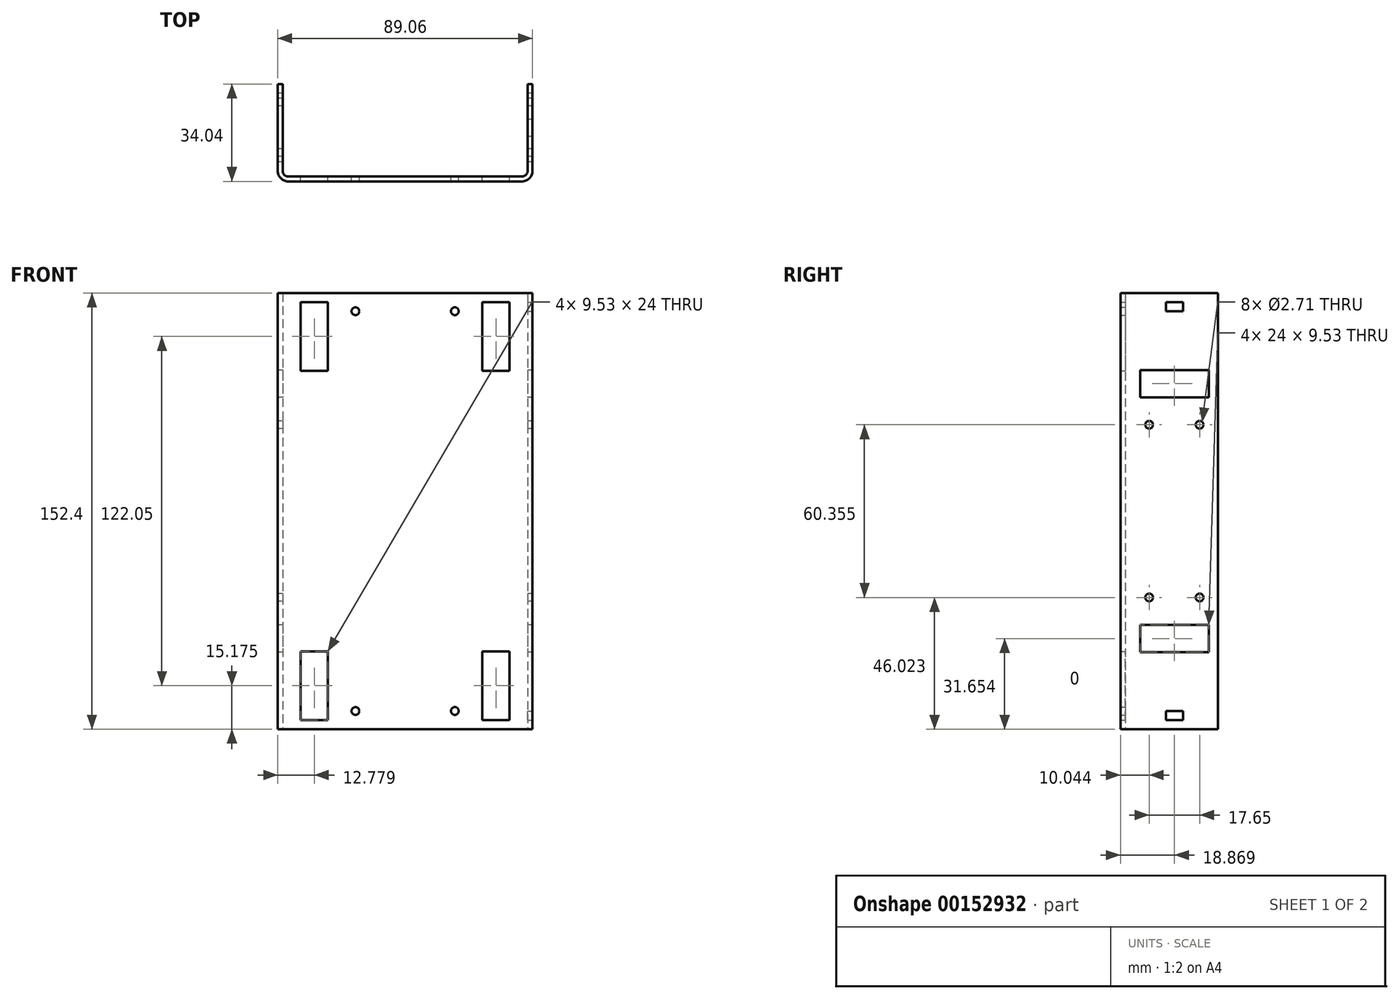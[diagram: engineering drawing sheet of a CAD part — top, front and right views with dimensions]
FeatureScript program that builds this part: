
annotation { "Feature Type Name" : "Feature", "Feature Type Description" : "" }
export const myFeature = defineFeature(function(context is Context, id is Id, definition is map)
    precondition{}
    {
        {
            var Q0;
            Q0=qCreatedBy(makeId("Top.planeOp"),FACE);
            var sketch = newSketch(context, id + "F0", { "sketchPlane" : qUnion([Q0])});
            skLineSegment(sketch, "E0.bottom", {"start": v(0, 0) * mm, "end": v(-85.64, 0) * mm});
            skLineSegment(sketch, "E0.top", {"start": v(1.7, -1.7) * mm, "end": v(-87.35, -1.7) * mm});
            skLineSegment(sketch, "E1.top", {"start": v(-85.64, 32.33) * mm, "end": v(-87.35, 32.33) * mm});
            skLineSegment(sketch, "E1.left", {"start": v(-85.64, 0) * mm, "end": v(-85.64, 32.33) * mm});
            skLineSegment(sketch, "E1.right", {"start": v(-87.35, -1.7) * mm, "end": v(-87.35, 32.33) * mm});
            skLineSegment(sketch, "E2.top", {"start": v(0, 32.33) * mm, "end": v(1.7, 32.33) * mm});
            skLineSegment(sketch, "E2.left", {"start": v(0, 0) * mm, "end": v(0, 32.33) * mm});
            skLineSegment(sketch, "E2.right", {"start": v(1.7, -1.7) * mm, "end": v(1.7, 32.33) * mm});
            skLineSegment(sketch, "E3", {"start": v(-42.82, 0) * mm, "end": v(-42.82, -1.7) * mm, "construction": true});
            skSolve(sketch);
        }
        {
            var Q0;
            Q0=qSketchRegion(id+"F0",true);
            extrude(context, id + "F1", {"entities" : qUnion([Q0]), "depth" : 152.4 * mm});
        }
        {
            var Q0;
            Q0=makeQuery(id+"FcdIcV9w6YY9zah_1.opExtrude","CAP_EDGE",EDGE,{"disambiguationData":[OSD([sQuery(id+"FU7sgaIbCbRhSfr_1.wireOp",EDGE,"F29Sxc5V-O2cl-wjtz-gx5o-reTTBG7m1pNU.top")])],"isStart":true});
            var Q1;
            Q1=makeQuery(id+"FcdIcV9w6YY9zah_1.opExtrude","CAP_EDGE",EDGE,{"disambiguationData":[OSD([sQuery(id+"FU7sgaIbCbRhSfr_1.wireOp",EDGE,"yv2bQU74-Eht6-uYuo-WBF2-3C4kyuaz0slr.top")])],"isStart":true});
            var Q2;
            Q2=makeQuery(id+"F1.opExtrude","SWEPT_EDGE",EDGE,{"disambiguationData":[OSD([sQuery(id+"F0.wireOp",EDGE,"E0.bottom"),sQuery(id+"F0.wireOp",EDGE,"E2.left")])]});
            var Q3;
            Q3=makeQuery(id+"F1.opExtrude","SWEPT_EDGE",EDGE,{"disambiguationData":[OSD([sQuery(id+"F0.wireOp",EDGE,"E0.bottom"),sQuery(id+"F0.wireOp",EDGE,"E1.left")])]});
            fillet(context, id + "F2", {"entities" : qUnion([Q0, Q1, Q2, Q3]), "radius" : 1.98 * mm, "tangentPropagation" : true, "allowEdgeOverflow" : false});
        }
        {
            var Q0;
            Q0=makeQuery(id+"FkwQQH4eT4IjhdK_1.opExtrude","CAP_EDGE",EDGE,{"disambiguationData":[OSD([sQuery(id+"FvDFSbhwMPyTNrQ_1.wireOp",EDGE,"223FG13h-YrEq-unoX-9EOi-DwKLLmwbrteD.top")])],"isStart":false});
            var Q1;
            Q1=makeQuery(id+"F1.opExtrude","SWEPT_EDGE",EDGE,{"disambiguationData":[OSD([sQuery(id+"F0.wireOp",EDGE,"E0.top"),sQuery(id+"F0.wireOp",EDGE,"E2.right")])]});
            var Q2;
            Q2=makeQuery(id+"F1.opExtrude","SWEPT_EDGE",EDGE,{"disambiguationData":[OSD([sQuery(id+"F0.wireOp",EDGE,"E0.top"),sQuery(id+"F0.wireOp",EDGE,"E1.right")])]});
            var Q3;
            Q3=makeQuery(id+"F2kHonbXZaQoFrR_1.opExtrude","CAP_EDGE",EDGE,{"disambiguationData":[OSD([sQuery(id+"FsAbJG8AZOSwdHE_1.wireOp",EDGE,"WRaIy3id-o2EU-qHqw-IwdC-eHQZRSiK4KpF.bottom")])],"isStart":false});
            fillet(context, id + "F3", {"entities" : qUnion([Q0, Q1, Q2, Q3]), "radius" : 3.7 * mm, "tangentPropagation" : true, "allowEdgeOverflow" : false});
        }
        {
            var Q0;
            Q0=makeQuery(id+"F1.opExtrude","SWEPT_FACE",FACE,{"disambiguationData":[OSD([sQuery(id+"F0.wireOp",EDGE,"E0.bottom")])]});
            var sketch = newSketch(context, id + "F4", { "sketchPlane" : qUnion([Q0])});
            skLineSegment(sketch, "E4", {"start": v(42.82, 0) * mm, "end": v(42.82, 152.4) * mm, "construction": true});
            skLineSegment(sketch, "E5.bottom", {"start": v(83.66, 0) * mm, "end": v(74.57, 0) * mm, "construction": true});
            skLineSegment(sketch, "E5.top", {"start": v(83.66, 15.17) * mm, "end": v(74.57, 15.17) * mm, "construction": true});
            skLineSegment(sketch, "E5.left", {"start": v(83.66, 0) * mm, "end": v(83.66, 15.17) * mm, "construction": true});
            skLineSegment(sketch, "E5.right", {"start": v(74.57, 0) * mm, "end": v(74.57, 15.17) * mm, "construction": true});
            skLineSegment(sketch, "E6.bottom", {"start": v(74.57, 15.18) * mm, "end": v(11.07, 15.18) * mm, "construction": true});
            skLineSegment(sketch, "E6.top", {"start": v(74.57, 137.22) * mm, "end": v(11.07, 137.22) * mm, "construction": true});
            skLineSegment(sketch, "E6.left", {"start": v(74.57, 15.17) * mm, "end": v(74.57, 137.23) * mm, "construction": true});
            skLineSegment(sketch, "E6.right", {"start": v(11.07, 15.18) * mm, "end": v(11.07, 137.22) * mm, "construction": true});
            skPoint(sketch, "E6.middle", {"position": v(42.82, 76.2) * mm});
            skLineSegment(sketch, "E7.bottom", {"start": v(69.8, 3.18) * mm, "end": v(79.34, 3.18) * mm});
            skLineSegment(sketch, "E7.top", {"start": v(69.8, 27.18) * mm, "end": v(79.34, 27.18) * mm});
            skLineSegment(sketch, "E7.left", {"start": v(69.8, 3.17) * mm, "end": v(69.8, 27.18) * mm});
            skLineSegment(sketch, "E7.right", {"start": v(79.34, 3.17) * mm, "end": v(79.34, 27.18) * mm});
            skPoint(sketch, "E7.middle", {"position": v(74.57, 15.17) * mm});
            skLineSegment(sketch, "E8.bottom", {"start": v(15.84, 3.18) * mm, "end": v(6.3, 3.18) * mm});
            skLineSegment(sketch, "E8.top", {"start": v(15.84, 27.18) * mm, "end": v(6.3, 27.18) * mm});
            skLineSegment(sketch, "E8.left", {"start": v(15.84, 3.18) * mm, "end": v(15.84, 27.18) * mm});
            skLineSegment(sketch, "E8.right", {"start": v(6.3, 3.18) * mm, "end": v(6.3, 27.18) * mm});
            skPoint(sketch, "E8.middle", {"position": v(11.07, 15.18) * mm});
            skLineSegment(sketch, "E9.bottom", {"start": v(6.3, 149.22) * mm, "end": v(15.84, 149.22) * mm});
            skLineSegment(sketch, "E9.top", {"start": v(6.3, 125.22) * mm, "end": v(15.84, 125.22) * mm});
            skLineSegment(sketch, "E9.left", {"start": v(6.3, 149.22) * mm, "end": v(6.3, 125.22) * mm});
            skLineSegment(sketch, "E9.right", {"start": v(15.84, 149.22) * mm, "end": v(15.84, 125.22) * mm});
            skPoint(sketch, "E9.middle", {"position": v(11.07, 137.22) * mm});
            skLineSegment(sketch, "E10.bottom", {"start": v(69.8, 149.23) * mm, "end": v(79.34, 149.23) * mm});
            skLineSegment(sketch, "E10.top", {"start": v(69.8, 125.23) * mm, "end": v(79.34, 125.23) * mm});
            skLineSegment(sketch, "E10.left", {"start": v(69.8, 149.23) * mm, "end": v(69.8, 125.23) * mm});
            skLineSegment(sketch, "E10.right", {"start": v(79.34, 149.23) * mm, "end": v(79.34, 125.23) * mm});
            skPoint(sketch, "E10.middle", {"position": v(74.57, 137.23) * mm});
            skLineSegment(sketch, "E11.bottom", {"start": v(60.2, 6.35) * mm, "end": v(25.44, 6.35) * mm, "construction": true});
            skLineSegment(sketch, "E11.top", {"start": v(60.2, 146.05) * mm, "end": v(25.44, 146.05) * mm, "construction": true});
            skLineSegment(sketch, "E11.left", {"start": v(60.2, 6.35) * mm, "end": v(60.2, 146.05) * mm, "construction": true});
            skLineSegment(sketch, "E11.right", {"start": v(25.44, 6.35) * mm, "end": v(25.44, 146.05) * mm, "construction": true});
            skLineSegment(sketch, "E12", {"start": v(69.8, 3.18) * mm, "end": v(60.2, 3.18) * mm, "construction": true});
            skLineSegment(sketch, "E13", {"start": v(60.2, 3.18) * mm, "end": v(60.2, 6.35) * mm, "construction": true});
            skCircle(sketch, "E14", {"center": v(60.2, 6.35) * mm, "radius": 1.35 * mm});
            skCircle(sketch, "E15", {"center": v(25.44, 6.35) * mm, "radius": 1.35 * mm});
            skCircle(sketch, "E16", {"center": v(25.44, 146.05) * mm, "radius": 1.35 * mm});
            skCircle(sketch, "E17", {"center": v(60.2, 146.05) * mm, "radius": 1.35 * mm});
            skSolve(sketch);
        }
        {
            var Q0;
            Q0 = qSketchRegion(id + "F4", true);
            var Q1;
            Q1=makeQuery(id+"F1.opExtrude","SWEPT_FACE",FACE,{"disambiguationData":[OSD([sQuery(id+"F0.wireOp",EDGE,"E0.top")])]});
            extrude(context, id + "F5", {"entities" : qUnion([Q0]), "operationType" : NewBodyOperationType.REMOVE, "endBound" : BoundingType.UP_TO_SURFACE, "oppositeDirection" : true, "endBoundEntityFace" : qUnion([Q1]), "depth" : 25.4 * mm});
        }
        {
            var Q0;
            Q0=makeQuery(id+"F1.opExtrude","SWEPT_FACE",FACE,{"disambiguationData":[OSD([sQuery(id+"F0.wireOp",EDGE,"E1.right")])]});
            var sketch = newSketch(context, id + "F6", { "sketchPlane" : qUnion([Q0])});
            skLineSegment(sketch, "E18", {"start": v(-1.98, 76.2) * mm, "end": v(-17.16, 76.2) * mm, "construction": true});
            skLineSegment(sketch, "E19.bottom", {"start": v(-5.16, 36.42) * mm, "end": v(-29.16, 36.42) * mm});
            skLineSegment(sketch, "E19.top", {"start": v(-5.16, 26.89) * mm, "end": v(-29.16, 26.89) * mm});
            skLineSegment(sketch, "E19.left", {"start": v(-5.16, 36.42) * mm, "end": v(-5.16, 26.89) * mm});
            skLineSegment(sketch, "E19.right", {"start": v(-29.16, 36.42) * mm, "end": v(-29.16, 26.89) * mm});
            skLineSegment(sketch, "E20.bottom", {"start": v(-5.16, 125.51) * mm, "end": v(-29.16, 125.51) * mm});
            skLineSegment(sketch, "E20.top", {"start": v(-5.16, 115.98) * mm, "end": v(-29.16, 115.98) * mm});
            skLineSegment(sketch, "E20.left", {"start": v(-5.16, 125.51) * mm, "end": v(-5.16, 115.98) * mm});
            skLineSegment(sketch, "E20.right", {"start": v(-29.16, 125.51) * mm, "end": v(-29.16, 115.98) * mm});
            skLineSegment(sketch, "E21", {"start": v(-17.16, 125.51) * mm, "end": v(-17.16, 26.89) * mm, "construction": true});
            skLineSegment(sketch, "E22.bottom", {"start": v(-25.98, 46.02) * mm, "end": v(-8.33, 46.02) * mm, "construction": true});
            skLineSegment(sketch, "E22.top", {"start": v(-25.98, 106.38) * mm, "end": v(-8.33, 106.38) * mm, "construction": true});
            skLineSegment(sketch, "E22.left", {"start": v(-25.98, 46.02) * mm, "end": v(-25.98, 106.38) * mm, "construction": true});
            skLineSegment(sketch, "E22.right", {"start": v(-8.33, 46.02) * mm, "end": v(-8.33, 106.38) * mm, "construction": true});
            skPoint(sketch, "E22.middle", {"position": v(-17.16, 76.2) * mm});
            skLineSegment(sketch, "E23", {"start": v(-25.98, 46.02) * mm, "end": v(-29.16, 46.02) * mm, "construction": true});
            skLineSegment(sketch, "E24", {"start": v(-29.16, 46.02) * mm, "end": v(-29.16, 36.42) * mm, "construction": true});
            skCircle(sketch, "E25", {"center": v(-25.98, 46.02) * mm, "radius": 1.35 * mm});
            skCircle(sketch, "E26", {"center": v(-25.98, 106.38) * mm, "radius": 1.35 * mm});
            skCircle(sketch, "E27", {"center": v(-8.33, 106.38) * mm, "radius": 1.35 * mm});
            skCircle(sketch, "E28", {"center": v(-8.33, 46.02) * mm, "radius": 1.35 * mm});
            skPoint(sketch, "E29", {"position": v(-29.16, 120.75) * mm});
            skPoint(sketch, "E30", {"position": v(-29.16, 31.65) * mm});
            skSolve(sketch);
        }
        {
            var Q0;
            Q0 = qSketchRegion(id + "F6", true);
            var Q1;
            Q1=makeQuery(id+"F1.opExtrude","SWEPT_FACE",FACE,{"disambiguationData":[OSD([sQuery(id+"F0.wireOp",EDGE,"E2.right")])]});
            extrude(context, id + "F7", {"entities" : qUnion([Q0]), "operationType" : NewBodyOperationType.REMOVE, "endBound" : BoundingType.UP_TO_SURFACE, "oppositeDirection" : true, "endBoundEntityFace" : qUnion([Q1]), "depth" : 25.4 * mm});
        }
        {
            var Q0;
            Q0=makeQuery(id+"F1.opExtrude","SWEPT_FACE",FACE,{"disambiguationData":[OSD([sQuery(id+"F0.wireOp",EDGE,"E2.right")])]});
            var sketch = newSketch(context, id + "F8", { "sketchPlane" : qUnion([Q0])});
            skLineSegment(sketch, "E31", {"start": v(17.16, 152.4) * mm, "end": v(17.16, 149.22) * mm, "construction": true});
            skLineSegment(sketch, "E32", {"start": v(17.16, 0) * mm, "end": v(17.16, 3.18) * mm, "construction": true});
            skLineSegment(sketch, "E33.bottom", {"start": v(14.16, 3.18) * mm, "end": v(20.16, 3.18) * mm});
            skLineSegment(sketch, "E33.top", {"start": v(14.16, 6.35) * mm, "end": v(20.16, 6.35) * mm});
            skLineSegment(sketch, "E33.left", {"start": v(14.16, 3.18) * mm, "end": v(14.16, 6.35) * mm});
            skLineSegment(sketch, "E33.right", {"start": v(20.16, 3.18) * mm, "end": v(20.16, 6.35) * mm});
            skLineSegment(sketch, "E34.bottom", {"start": v(14.16, 149.22) * mm, "end": v(20.16, 149.22) * mm});
            skLineSegment(sketch, "E34.top", {"start": v(14.16, 146.05) * mm, "end": v(20.16, 146.05) * mm});
            skLineSegment(sketch, "E34.left", {"start": v(14.16, 149.22) * mm, "end": v(14.16, 146.05) * mm});
            skLineSegment(sketch, "E34.right", {"start": v(20.16, 149.22) * mm, "end": v(20.16, 146.05) * mm});
            skSolve(sketch);
        }
        {
            var Q0;
            Q0 = qSketchRegion(id + "F8", true);
            var Q1;
            Q1=makeQuery(id+"F1.opExtrude","SWEPT_FACE",FACE,{"disambiguationData":[OSD([sQuery(id+"F0.wireOp",EDGE,"E2.left")])]});
            extrude(context, id + "F9", {"entities" : qUnion([Q0]), "operationType" : NewBodyOperationType.REMOVE, "endBound" : BoundingType.UP_TO_SURFACE, "oppositeDirection" : true, "endBoundEntityFace" : qUnion([Q1]), "depth" : 25.4 * mm});
        }
    });
